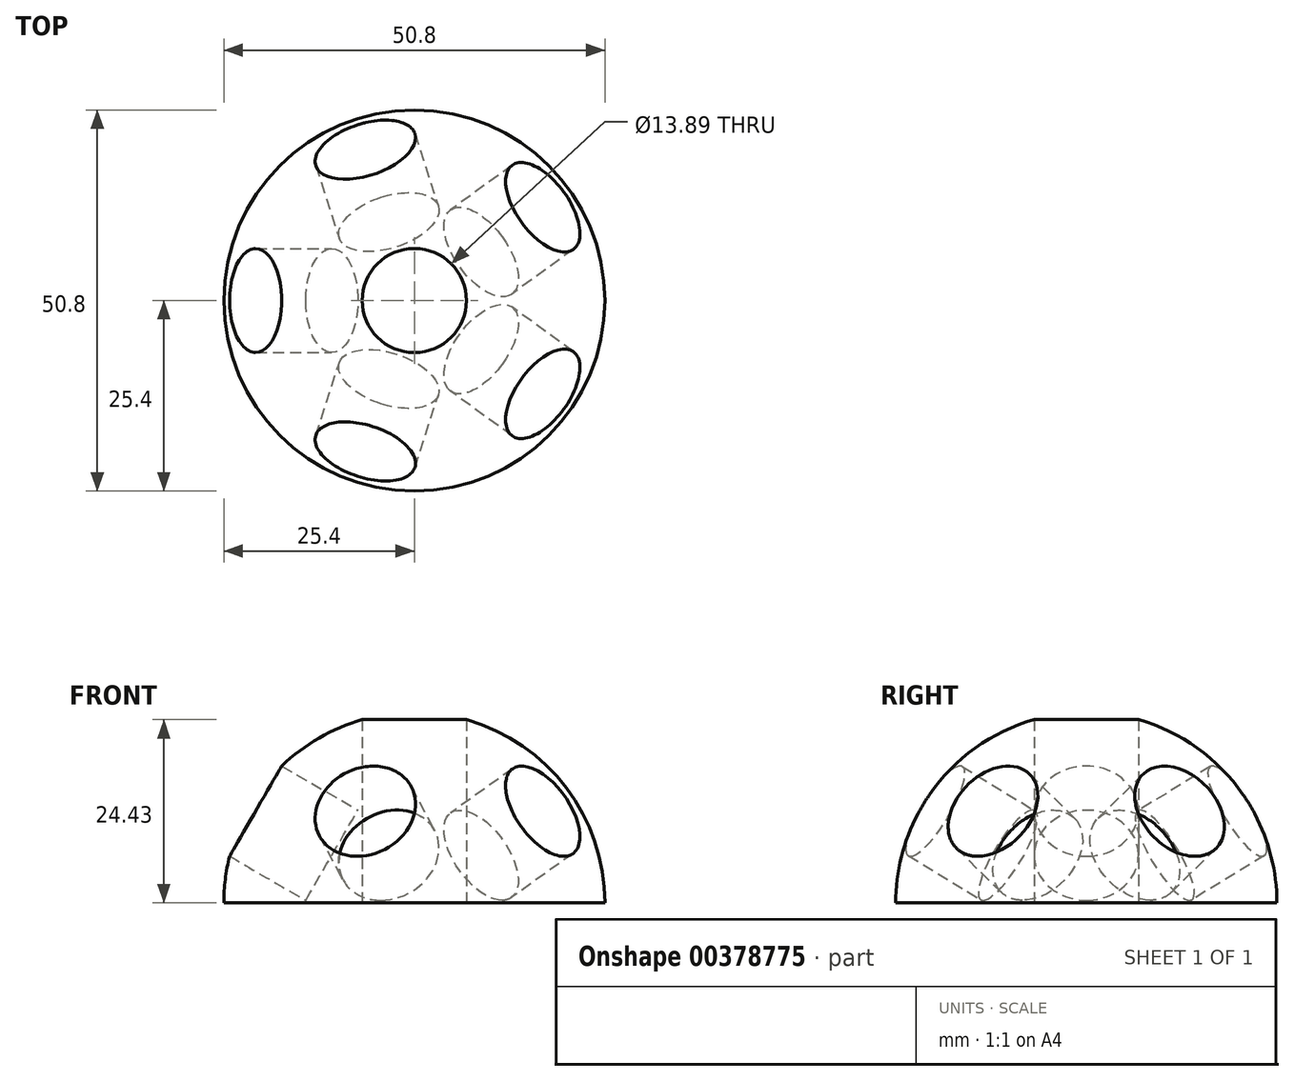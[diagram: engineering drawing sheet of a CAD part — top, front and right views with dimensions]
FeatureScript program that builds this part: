
annotation { "Feature Type Name" : "Feature", "Feature Type Description" : "" }
export const myFeature = defineFeature(function(context is Context, id is Id, definition is map)
    precondition{}
    {
        {
            var Q0;
            Q0=qCreatedBy(makeId("Top.planeOp"),FACE);
            var sketch = newSketch(context, id + "F0", { "sketchPlane" : qUnion([Q0])});
            skArc(sketch, "E0", {"start": v(0, -25.4) * mm, "mid": v(25.4, 0) * mm, "end": v(0, 25.4) * mm});
            skLineSegment(sketch, "E1", {"start": v(0, 0) * mm, "end": v(0, 25.4) * mm});
            skLineSegment(sketch, "E2", {"start": v(0, 25.4) * mm, "end": v(0, -39.9) * mm});
            skPoint(sketch, "E2.endSnap0", {"position": v(0, 12.7) * mm});
            skLineSegment(sketch, "E3", {"start": v(0, -39.9) * mm, "end": v(0, 0) * mm});
            skSolve(sketch);
        }
        {
            var Q0;
            {var subQ0=sQuery(id+"F0.wireOp",EDGE,"E0");Q0=makeQuery(id+"F0.imprint","IMPRINT",FACE,{"disambiguationData":[TD([[makeQuery(id+"F0.imprint","IMPRINT",EDGE,{"derivedFrom":subQ0}),1.0]])]});}
            var Q1;
            Q1=sQuery(id+"F0.wireOp",EDGE,"E3");
            revolve(context, id + "F1", {"entities" : qUnion([Q0]), "axis" : qUnion([Q1]), "revolveType" : RevolveType.ONE_DIRECTION, "oppositeDirection" : true, "angle" : 180 * degree});
        }
        {
            var Q0;
            Q0=makeQuery(id+"F1.opRevolve","CAP_FACE",FACE,{"disambiguationData":[OSD([sQuery(id+"F0.wireOp",EDGE,"E0"),sQuery(id+"F0.wireOp",EDGE,"E2"),sQuery(id+"F0.wireOp",EDGE,"E3")])],"isStart":true});
            var sketch = newSketch(context, id + "F2", { "sketchPlane" : qUnion([Q0])});
            skCircle(sketch, "E4", {"center": v(0, 0) * mm, "radius": 6.95 * mm});
            skLineSegment(sketch, "E5", {"start": v(0, -25.4) * mm, "end": v(0, 24.17) * mm});
            skSolve(sketch);
        }
        {
            var Q0;
            Q0=makeQuery(id+"F2.imprint","IMPRINT",FACE,{"disambiguationData":[TD([[makeQuery(id+"F2.imprint","IMPRINT",EDGE,{"derivedFrom":sQuery(id+"F2.wireOp",EDGE,"E4")}),1.0]])]});
            extrude(context, id + "F3", {"entities" : qUnion([Q0]), "oppositeDirection" : true, "depth" : 38.1 * mm});
        }
        {
            var Q0;
            Q0=makeQuery(id+"F3.opExtrude","SWEPT_BODY",BODY,{"disambiguationData":[OSD([sQuery(id+"F2.wireOp",EDGE,"E4")])]});
            var Q1;
            Q1=sQuery(id+"F2.wireOp",EDGE,"E5");
            transform(context, id + "F4", {"entities" : qUnion([Q0]), "transformType" : TransformType.ROTATION, "transformAxis" : qUnion([Q1]), "angle" : 60 * degree, "makeCopy" : true});
        }
        {
            var Q0;
            Q0=qCreatedBy(makeId("Front.planeOp"),FACE);
            var sketch = newSketch(context, id + "F5", { "sketchPlane" : qUnion([Q0])});
            skLineSegment(sketch, "E6", {"start": v(0, 41.97) * mm, "end": v(0, -20.58) * mm});
            skSolve(sketch);
        }
        {
            var Q0;
            Q0=qCreatedBy(makeId("Front.planeOp"),FACE);
            var sketch = newSketch(context, id + "F6", { "sketchPlane" : qUnion([Q0])});
            skLineSegment(sketch, "E7", {"start": v(0, 0) * mm, "end": v(-43.26, 24.98) * mm});
            skPoint(sketch, "E8.orphan", {"position": v(-33, 19.05) * mm});
            skSolve(sketch);
        }
        {
            var Q0;
            Q0=makeQuery(id+"F4.opPattern","COPY",BODY,{"derivedFrom":makeQuery(id+"F3.opExtrude","SWEPT_BODY",BODY,{"disambiguationData":[OSD([sQuery(id+"F2.wireOp",EDGE,"E4")])]}),"instanceName":"1"});
            var Q1;
            Q1=sQuery(id+"F6.wireOp",EDGE,"E7");
            var Q2;
            Q2=sQuery(id+"F6.wireOp",EDGE,"E7");
            transform(context, id + "F7", {"entities" : qUnion([Q0]), "transformType" : TransformType.TRANSLATION_DISTANCE, "transformDirection" : qUnion([Q2]), "distance" : 12.7 * mm, "makeCopy" : false});
        }
        {
            var Q0;
            Q0=makeQuery(id+"F4.opPattern","COPY",BODY,{"derivedFrom":makeQuery(id+"F3.opExtrude","SWEPT_BODY",BODY,{"disambiguationData":[OSD([sQuery(id+"F2.wireOp",EDGE,"E4")])]}),"instanceName":"1"});
            var Q1;
            Q1=sQuery(id+"F5.wireOp",EDGE,"E6");
            circularPattern(context, id + "F8", {"entities" : qUnion([Q0]), "axis" : qUnion([Q1]), "angle" : 360 * degree, "instanceCount" : 5, "equalSpace" : true});
        }
        {
            var Q0;
            Q0=makeQuery(id+"F8.opPattern","COPY",BODY,{"derivedFrom":makeQuery(id+"F4.opPattern","COPY",BODY,{"derivedFrom":makeQuery(id+"F3.opExtrude","SWEPT_BODY",BODY,{"disambiguationData":[OSD([sQuery(id+"F2.wireOp",EDGE,"E4")])]}),"instanceName":"1"}),"instanceName":"1"});
            var Q1;
            Q1=makeQuery(id+"F8.opPattern","COPY",BODY,{"derivedFrom":makeQuery(id+"F4.opPattern","COPY",BODY,{"derivedFrom":makeQuery(id+"F3.opExtrude","SWEPT_BODY",BODY,{"disambiguationData":[OSD([sQuery(id+"F2.wireOp",EDGE,"E4")])]}),"instanceName":"1"}),"instanceName":"2"});
            var Q2;
            Q2=makeQuery(id+"F8.opPattern","COPY",BODY,{"derivedFrom":makeQuery(id+"F4.opPattern","COPY",BODY,{"derivedFrom":makeQuery(id+"F3.opExtrude","SWEPT_BODY",BODY,{"disambiguationData":[OSD([sQuery(id+"F2.wireOp",EDGE,"E4")])]}),"instanceName":"1"}),"instanceName":"3"});
            var Q3;
            Q3=makeQuery(id+"F8.opPattern","COPY",BODY,{"derivedFrom":makeQuery(id+"F4.opPattern","COPY",BODY,{"derivedFrom":makeQuery(id+"F3.opExtrude","SWEPT_BODY",BODY,{"disambiguationData":[OSD([sQuery(id+"F2.wireOp",EDGE,"E4")])]}),"instanceName":"1"}),"instanceName":"4"});
            var Q4;
            Q4=makeQuery(id+"F4.opPattern","COPY",BODY,{"derivedFrom":makeQuery(id+"F3.opExtrude","SWEPT_BODY",BODY,{"disambiguationData":[OSD([sQuery(id+"F2.wireOp",EDGE,"E4")])]}),"instanceName":"1"});
            var Q5;
            Q5=makeQuery(id+"F3.opExtrude","SWEPT_BODY",BODY,{"disambiguationData":[OSD([sQuery(id+"F2.wireOp",EDGE,"E4")])]});
            var Q6;
            Q6=makeQuery(id+"F1.opRevolve","SWEPT_BODY",BODY,{"disambiguationData":[OSD([sQuery(id+"F0.wireOp",EDGE,"E0"),sQuery(id+"F0.wireOp",EDGE,"E2"),sQuery(id+"F0.wireOp",EDGE,"E3")])]});
            booleanBodies(context, id + "F9", {"operationType" : BooleanOperationType.SUBTRACTION, "tools" : qUnion([Q0, Q1, Q2, Q3, Q4, Q5]), "targets" : qUnion([Q6])});
        }
    });
